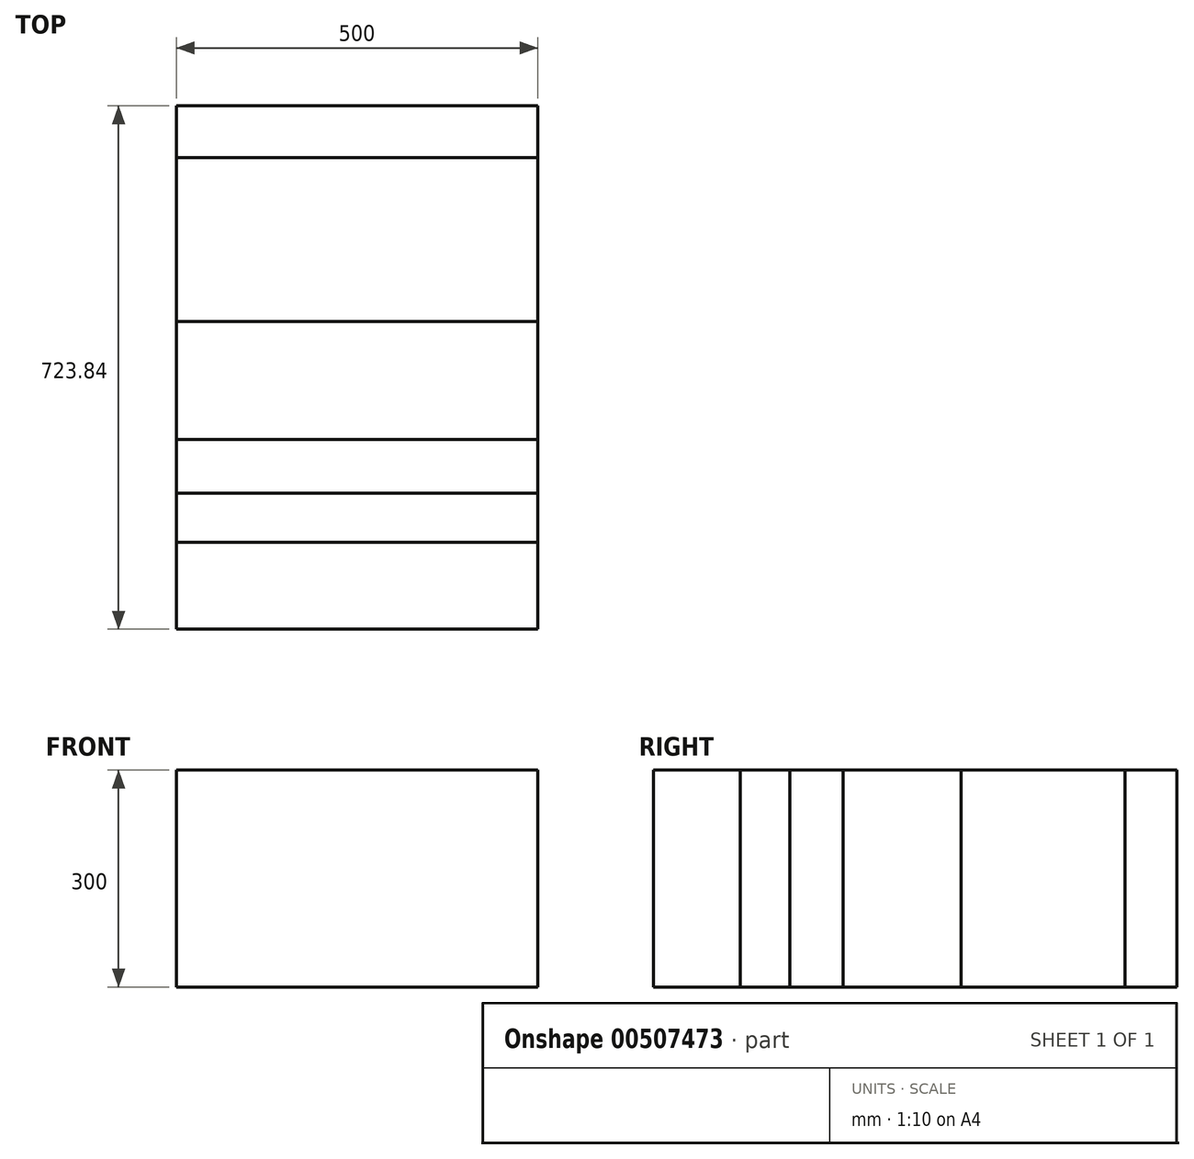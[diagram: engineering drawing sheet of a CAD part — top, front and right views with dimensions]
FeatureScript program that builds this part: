
annotation { "Feature Type Name" : "Feature", "Feature Type Description" : "" }
export const myFeature = defineFeature(function(context is Context, id is Id, definition is map)
    precondition{}
    {
        {
            var Q0;
            Q0=qCreatedBy(makeId("Right.planeOp"),FACE);
            var sketch = newSketch(context, id + "F0", { "sketchPlane" : qUnion([Q0])});
            skLineSegment(sketch, "E0.bottom", {"start": v(0, 217.8) * mm, "end": v(-71.76, 217.8) * mm});
            skLineSegment(sketch, "E0.top", {"start": v(0, -82.2) * mm, "end": v(-71.76, -82.2) * mm});
            skLineSegment(sketch, "E0.left", {"start": v(0, 217.8) * mm, "end": v(0, -82.2) * mm});
            skLineSegment(sketch, "E0.right", {"start": v(-71.76, 217.8) * mm, "end": v(-71.76, -82.2) * mm});
            skSolve(sketch);
        }
        {
            var Q0;
            Q0 = qSketchRegion(id + "F0", true);
            var sketch = newSketch(context, id + "F1", { "sketchPlane" : qUnion([Q0])});
            skLineSegment(sketch, "E1.bottom", {"start": v(-298.44, 217.8) * mm, "end": v(-71.76, 217.8) * mm});
            skLineSegment(sketch, "E1.top", {"start": v(-298.44, -82.2) * mm, "end": v(-71.76, -82.2) * mm});
            skLineSegment(sketch, "E1.left", {"start": v(-298.44, 217.8) * mm, "end": v(-298.44, -82.2) * mm});
            skLineSegment(sketch, "E1.right", {"start": v(-71.76, 217.8) * mm, "end": v(-71.76, -82.2) * mm});
            skLineSegment(sketch, "E2.bottom", {"start": v(-298.44, 217.8) * mm, "end": v(-461.65, 217.8) * mm});
            skLineSegment(sketch, "E2.top", {"start": v(-298.44, -82.2) * mm, "end": v(-461.65, -82.2) * mm});
            skLineSegment(sketch, "E2.right", {"start": v(-461.65, 217.8) * mm, "end": v(-461.65, -82.2) * mm});
            skLineSegment(sketch, "E3.bottom", {"start": v(-461.65, 217.8) * mm, "end": v(-535.58, 217.8) * mm});
            skLineSegment(sketch, "E3.top", {"start": v(-461.65, -82.2) * mm, "end": v(-535.58, -82.2) * mm});
            skLineSegment(sketch, "E3.right", {"start": v(-535.58, 217.8) * mm, "end": v(-535.58, -82.2) * mm});
            skLineSegment(sketch, "E4.bottom", {"start": v(-535.58, 217.8) * mm, "end": v(-603.68, 217.8) * mm});
            skLineSegment(sketch, "E4.top", {"start": v(-535.58, -82.2) * mm, "end": v(-603.68, -82.2) * mm});
            skLineSegment(sketch, "E4.right", {"start": v(-603.68, 217.8) * mm, "end": v(-603.68, -82.2) * mm});
            skLineSegment(sketch, "E5.bottom", {"start": v(-603.68, 217.8) * mm, "end": v(-723.84, 217.8) * mm});
            skLineSegment(sketch, "E5.top", {"start": v(-603.68, -82.2) * mm, "end": v(-723.84, -82.2) * mm});
            skLineSegment(sketch, "E5.right", {"start": v(-723.84, 217.8) * mm, "end": v(-723.84, -82.2) * mm});
            skSolve(sketch);
        }
        {
            var Q0;
            Q0=makeQuery(id+"F1.imprint","IMPRINT",FACE,{"disambiguationData":[TD([[makeQuery(id+"F1.imprint","IMPRINT",EDGE,{"derivedFrom":sQuery(id+"F1.wireOp",EDGE,"E2.bottom")}),1.0]])]});
            extrude(context, id + "F2", {"entities" : qUnion([Q0]), "depth" : 500 * mm, "symmetric" : true});
        }
        {
            var Q0;
            Q0=makeQuery(id+"F1.imprint","IMPRINT",FACE,{"disambiguationData":[TD([[makeQuery(id+"F1.imprint","IMPRINT",EDGE,{"derivedFrom":sQuery(id+"F1.wireOp",EDGE,"E3.bottom")}),1.0]])]});
            extrude(context, id + "F3", {"entities" : qUnion([Q0]), "depth" : 500 * mm, "symmetric" : true});
        }
        {
            var Q0;
            Q0=makeQuery(id+"F1.imprint","IMPRINT",FACE,{"disambiguationData":[TD([[makeQuery(id+"F1.imprint","IMPRINT",EDGE,{"derivedFrom":sQuery(id+"F1.wireOp",EDGE,"E4.bottom")}),1.0]])]});
            extrude(context, id + "F4", {"entities" : qUnion([Q0]), "depth" : 500 * mm, "symmetric" : true});
        }
        {
            var Q0;
            Q0=makeQuery(id+"F1.imprint","IMPRINT",FACE,{"disambiguationData":[TD([[makeQuery(id+"F1.imprint","IMPRINT",EDGE,{"derivedFrom":sQuery(id+"F1.wireOp",EDGE,"E5.bottom")}),1.0]])]});
            extrude(context, id + "F5", {"entities" : qUnion([Q0]), "depth" : 500 * mm, "symmetric" : true});
        }
        {
            var Q0;
            Q0=makeQuery(id+"F0.imprint","IMPRINT",FACE,{"disambiguationData":[TD([[makeQuery(id+"F0.imprint","IMPRINT",EDGE,{"derivedFrom":sQuery(id+"F0.wireOp",EDGE,"E0.bottom")}),1.0]])]});
            extrude(context, id + "F6", {"entities" : qUnion([Q0]), "depth" : 500 * mm, "symmetric" : true});
        }
        {
            var Q0;
            Q0=qCreatedBy(makeId("Right.planeOp"),FACE);
            var sketch = newSketch(context, id + "F7", { "sketchPlane" : qUnion([Q0])});
            skLineSegment(sketch, "E6", {"start": v(-544.73, 482.58) * mm, "end": v(-544.5, 482.58) * mm});
            skLineSegment(sketch, "E7", {"start": v(-544.48, 482.58) * mm, "end": v(-544.48, 482.34) * mm});
            skLineSegment(sketch, "E8", {"start": v(-544.48, 482.34) * mm, "end": v(-544.26, 482.59) * mm});
            skLineSegment(sketch, "E9", {"start": v(-543.41, 479.22) * mm, "end": v(-543.41, 479.22) * mm});
            skLineSegment(sketch, "E10", {"start": v(148.6, 413.4) * mm, "end": v(148.6, 524.4) * mm});
            skLineSegment(sketch, "E11", {"start": v(-455.02, 371.89) * mm, "end": v(-455.02, 520.96) * mm, "construction": true});
            skLineSegment(sketch, "E12", {"start": v(-386.58, 391.24) * mm, "end": v(-386.58, 519.74) * mm, "construction": true});
            skLineSegment(sketch, "E13", {"start": v(-537.77, 522.8) * mm, "end": v(-455.02, 520.96) * mm});
            skLineSegment(sketch, "E14", {"start": v(-574.7, 391.51) * mm, "end": v(-455.02, 391.16) * mm});
            skLineSegment(sketch, "E15", {"start": v(-149.14, 397.35) * mm, "end": v(76.9, 404.1) * mm});
            skLineSegment(sketch, "E16", {"start": v(185.78, 508.4) * mm, "end": v(186.03, 508.41) * mm});
            skLineSegment(sketch, "E17", {"start": v(185.9, 517.88) * mm, "end": v(185.9, 518.37) * mm});
            skLineSegment(sketch, "E18", {"start": v(185.9, 518.37) * mm, "end": v(185.64, 518.86) * mm});
            skLineSegment(sketch, "E19", {"start": v(185.64, 518.86) * mm, "end": v(185.4, 519.1) * mm});
            skLineSegment(sketch, "E20", {"start": v(185.4, 519.1) * mm, "end": v(185.16, 519.35) * mm});
            skLineSegment(sketch, "E21", {"start": v(186, 509) * mm, "end": v(185.9, 517.88) * mm});
            skLineSegment(sketch, "E22", {"start": v(184.81, 508.4) * mm, "end": v(179.48, 507.6) * mm});
            skLineSegment(sketch, "E23", {"start": v(179.48, 507.6) * mm, "end": v(174.38, 506.54) * mm});
            skLineSegment(sketch, "E24", {"start": v(174.38, 506.54) * mm, "end": v(169.53, 505.25) * mm});
            skLineSegment(sketch, "E25", {"start": v(169.53, 505.25) * mm, "end": v(164.46, 503.7) * mm});
            skLineSegment(sketch, "E26", {"start": v(184.81, 508.4) * mm, "end": v(185.06, 508.4) * mm});
            skLineSegment(sketch, "E27", {"start": v(185.06, 508.4) * mm, "end": v(185.3, 508.65) * mm});
            skLineSegment(sketch, "E28", {"start": v(185.3, 508.65) * mm, "end": v(185.77, 508.9) * mm});
            skLineSegment(sketch, "E29", {"start": v(185.77, 508.9) * mm, "end": v(185.77, 509.15) * mm});
            skLineSegment(sketch, "E30", {"start": v(185.77, 509.15) * mm, "end": v(186.01, 509.4) * mm});
            skLineSegment(sketch, "E31", {"start": v(186.01, 509.4) * mm, "end": v(186, 509.9) * mm});
            skLineSegment(sketch, "E32", {"start": v(164.46, 503.7) * mm, "end": v(161.07, 502.19) * mm});
            skLineSegment(sketch, "E33", {"start": v(161.07, 502.19) * mm, "end": v(157.7, 500.17) * mm});
            skLineSegment(sketch, "E34", {"start": v(157.7, 500.17) * mm, "end": v(154.55, 497.67) * mm});
            skLineSegment(sketch, "E35", {"start": v(154.55, 497.67) * mm, "end": v(152.17, 494.68) * mm});
            skLineSegment(sketch, "E36", {"start": v(152.17, 494.68) * mm, "end": v(150, 491.44) * mm});
            skLineSegment(sketch, "E37", {"start": v(150, 491.44) * mm, "end": v(148.6, 487.7) * mm});
            skLineSegment(sketch, "E38", {"start": v(185.16, 519.35) * mm, "end": v(181.97, 520.8) * mm});
            skLineSegment(sketch, "E39", {"start": v(181.97, 520.8) * mm, "end": v(179.05, 522) * mm});
            skLineSegment(sketch, "E40", {"start": v(179.05, 522) * mm, "end": v(175.64, 522.7) * mm});
            skLineSegment(sketch, "E41", {"start": v(175.64, 522.7) * mm, "end": v(172.47, 523.37) * mm});
            skLineSegment(sketch, "E42", {"start": v(172.47, 523.37) * mm, "end": v(169.07, 523.58) * mm});
            skLineSegment(sketch, "E43", {"start": v(169.07, 523.58) * mm, "end": v(165.65, 523.7) * mm});
            skLineSegment(sketch, "E44", {"start": v(-149.14, 397.35) * mm, "end": v(-149.14, 534.21) * mm, "construction": true});
            skLineSegment(sketch, "E45", {"start": v(-120.5, 533.08) * mm, "end": v(-45.95, 597.87) * mm});
            skLineSegment(sketch, "E46", {"start": v(64.59, 702.58) * mm, "end": v(101.77, 703.03) * mm});
            skLineSegment(sketch, "E47", {"start": v(95.44, 664.45) * mm, "end": v(101.77, 703.03) * mm});
            skLineSegment(sketch, "E48", {"start": v(61.9, 664.05) * mm, "end": v(95.44, 664.45) * mm});
            skLineSegment(sketch, "E49", {"start": v(61.9, 664.05) * mm, "end": v(66.93, 528.67) * mm});
            skLineSegment(sketch, "E50", {"start": v(66.93, 528.67) * mm, "end": v(118.28, 529.3) * mm});
            skLineSegment(sketch, "E51", {"start": v(-59.6, 601.16) * mm, "end": v(-53.01, 600.5) * mm});
            skLineSegment(sketch, "E52", {"start": v(-53.01, 600.5) * mm, "end": v(-46.7, 600.08) * mm});
            skLineSegment(sketch, "E53", {"start": v(-59.6, 601.16) * mm, "end": v(-59.38, 603.63) * mm});
            skLineSegment(sketch, "E54", {"start": v(-76.39, 603.67) * mm, "end": v(-59.38, 603.63) * mm});
            skLineSegment(sketch, "E55", {"start": v(-76.36, 601.2) * mm, "end": v(-59.35, 601.16) * mm});
            skLineSegment(sketch, "E56", {"start": v(-76.36, 601.2) * mm, "end": v(-76.39, 603.67) * mm});
            skLineSegment(sketch, "E57", {"start": v(-48.46, 605.49) * mm, "end": v(-51.38, 605.45) * mm});
            skLineSegment(sketch, "E58", {"start": v(-51.38, 605.45) * mm, "end": v(-54.06, 605.18) * mm});
            skLineSegment(sketch, "E59", {"start": v(-54.06, 605.18) * mm, "end": v(-56.71, 604.4) * mm});
            skLineSegment(sketch, "E60", {"start": v(-56.71, 604.4) * mm, "end": v(-59.38, 603.63) * mm});
            skLineSegment(sketch, "E61", {"start": v(-47.5, 606) * mm, "end": v(64.59, 702.58) * mm});
            skLineSegment(sketch, "E62", {"start": v(-48.46, 605.49) * mm, "end": v(-48.23, 605.5) * mm});
            skLineSegment(sketch, "E63", {"start": v(-48.23, 605.5) * mm, "end": v(-47.98, 605.74) * mm});
            skLineSegment(sketch, "E64", {"start": v(-47.98, 605.74) * mm, "end": v(-47.74, 605.75) * mm});
            skLineSegment(sketch, "E65", {"start": v(-47.74, 605.75) * mm, "end": v(-47.5, 606) * mm});
            skLineSegment(sketch, "E66", {"start": v(-45.95, 597.87) * mm, "end": v(-45.7, 598.37) * mm});
            skLineSegment(sketch, "E67", {"start": v(-45.7, 598.37) * mm, "end": v(-45.71, 598.61) * mm});
            skLineSegment(sketch, "E68", {"start": v(-45.71, 598.61) * mm, "end": v(-45.72, 598.86) * mm});
            skLineSegment(sketch, "E69", {"start": v(-45.72, 598.86) * mm, "end": v(-45.72, 599.35) * mm});
            skLineSegment(sketch, "E70", {"start": v(-45.72, 599.35) * mm, "end": v(-45.97, 599.6) * mm});
            skLineSegment(sketch, "E71", {"start": v(-45.97, 599.6) * mm, "end": v(-46.2, 599.84) * mm});
            skLineSegment(sketch, "E72", {"start": v(-46.2, 599.84) * mm, "end": v(-46.45, 600.08) * mm});
            skLineSegment(sketch, "E73", {"start": v(-46.45, 600.08) * mm, "end": v(-46.7, 600.08) * mm});
            skLineSegment(sketch, "E74", {"start": v(35.26, 677.3) * mm, "end": v(97.67, 678.05) * mm});
            skLineSegment(sketch, "E75", {"start": v(-823.38, 455.9) * mm, "end": v(148.6, 455.9) * mm, "construction": true});
            skLineSegment(sketch, "E76", {"start": v(76.9, 404.1) * mm, "end": v(76.9, 492.42) * mm, "construction": true});
            skLineSegment(sketch, "E77", {"start": v(-665.56, 391.08) * mm, "end": v(-574.7, 391.51) * mm});
            skLineSegment(sketch, "E78", {"start": v(-455.02, 391.16) * mm, "end": v(-386.58, 391.24) * mm});
            skLineSegment(sketch, "E79", {"start": v(-386.58, 391.24) * mm, "end": v(-312.7, 393.12) * mm});
            skLineSegment(sketch, "E80", {"start": v(76.9, 404.1) * mm, "end": v(148.6, 413.4) * mm});
            skLineSegment(sketch, "E81", {"start": v(-120.54, 533.04) * mm, "end": v(-45.95, 597.87) * mm});
            skLineSegment(sketch, "E82", {"start": v(95.44, 664.45) * mm, "end": v(119.07, 524.64) * mm});
            skLineSegment(sketch, "E83", {"start": v(66.93, 528.67) * mm, "end": v(118.21, 529.3) * mm});
            skLineSegment(sketch, "E84", {"start": v(-312.7, 366.48) * mm, "end": v(-312.7, 519.05) * mm, "construction": true});
            skLineSegment(sketch, "E85", {"start": v(-454.68, 410.4) * mm, "end": v(-148.5, 415.81) * mm});
            skLineSegment(sketch, "E86", {"start": v(-455.05, 482.68) * mm, "end": v(-150.92, 495.96) * mm});
            skLineSegment(sketch, "E87", {"start": v(-573.21, 404.77) * mm, "end": v(-454.68, 410.4) * mm});
            skLineSegment(sketch, "E88", {"start": v(-564.23, 487.04) * mm, "end": v(-544.3, 487.03) * mm});
            skLineSegment(sketch, "E89", {"start": v(-544.3, 487.03) * mm, "end": v(-455.16, 491.8) * mm});
            skLineSegment(sketch, "E90", {"start": v(-455.16, 491.8) * mm, "end": v(-387.23, 501.75) * mm});
            skLineSegment(sketch, "E91", {"start": v(-564.19, 483.83) * mm, "end": v(-564.23, 487.04) * mm});
            skLineSegment(sketch, "E92", {"start": v(-563.19, 400.95) * mm, "end": v(-543.75, 401.43) * mm});
            skLineSegment(sketch, "E93", {"start": v(-563.19, 400.95) * mm, "end": v(-563.24, 404.9) * mm});
            skLineSegment(sketch, "E94", {"start": v(-543.75, 401.43) * mm, "end": v(-453.37, 403.26) * mm});
            skLineSegment(sketch, "E95", {"start": v(-453.37, 403.26) * mm, "end": v(-385.57, 403.83) * mm});
            skLineSegment(sketch, "E96", {"start": v(-385.57, 403.83) * mm, "end": v(-267.87, 398.33) * mm});
            skLineSegment(sketch, "E97", {"start": v(-387.23, 501.75) * mm, "end": v(-117.7, 502.53) * mm});
            skLineSegment(sketch, "E98", {"start": v(-117.7, 502.53) * mm, "end": v(76.9, 507.59) * mm});
            skLineSegment(sketch, "E99", {"start": v(76.9, 507.59) * mm, "end": v(184.81, 508.4) * mm});
            skLineSegment(sketch, "E100", {"start": v(-563.24, 405.39) * mm, "end": v(-564.19, 483.83) * mm});
            skLineSegment(sketch, "E101", {"start": v(-386.89, 493.86) * mm, "end": v(-313.11, 501.9) * mm});
            skLineSegment(sketch, "E102", {"start": v(-530.49, 469.18) * mm, "end": v(-533.38, 467.91) * mm});
            skLineSegment(sketch, "E103", {"start": v(-534.35, 467.66) * mm, "end": v(-535.3, 467.15) * mm});
            skLineSegment(sketch, "E104", {"start": v(-535.3, 467.15) * mm, "end": v(-537, 466.14) * mm});
            skLineSegment(sketch, "E105", {"start": v(-537.73, 465.89) * mm, "end": v(-539.9, 464.63) * mm});
            skLineSegment(sketch, "E106", {"start": v(-539.9, 464.63) * mm, "end": v(-540.39, 464.37) * mm});
            skLineSegment(sketch, "E107", {"start": v(-541.1, 463.87) * mm, "end": v(-543.76, 462.36) * mm});
            skLineSegment(sketch, "E108", {"start": v(-544.48, 461.86) * mm, "end": v(-546.9, 460.1) * mm});
            skLineSegment(sketch, "E109", {"start": v(-547.63, 459.6) * mm, "end": v(-548.83, 458.84) * mm});
            skLineSegment(sketch, "E110", {"start": v(-548.83, 458.84) * mm, "end": v(-550.02, 457.84) * mm});
            skLineSegment(sketch, "E111", {"start": v(-550.75, 457.1) * mm, "end": v(-552.92, 455.59) * mm});
            skLineSegment(sketch, "E112", {"start": v(-552.92, 455.59) * mm, "end": v(-553.16, 455.34) * mm});
            skLineSegment(sketch, "E113", {"start": v(-553.88, 454.59) * mm, "end": v(-556.04, 452.59) * mm});
            skLineSegment(sketch, "E114", {"start": v(-556.77, 452.09) * mm, "end": v(-558.68, 449.84) * mm});
            skLineSegment(sketch, "E115", {"start": v(-559.4, 449.1) * mm, "end": v(-560.36, 448.1) * mm});
            skLineSegment(sketch, "E116", {"start": v(-560.36, 448.1) * mm, "end": v(-561.3, 446.85) * mm});
            skLineSegment(sketch, "E117", {"start": v(-562.04, 446.12) * mm, "end": v(-563.7, 444.12) * mm});
            skLineSegment(sketch, "E118", {"start": v(-563.7, 444.12) * mm, "end": v(-561.98, 441.43) * mm});
            skLineSegment(sketch, "E119", {"start": v(-561.48, 440.7) * mm, "end": v(-561.23, 440.2) * mm});
            skLineSegment(sketch, "E120", {"start": v(-561.23, 440.2) * mm, "end": v(-559.51, 438.25) * mm});
            skLineSegment(sketch, "E121", {"start": v(-559.01, 437.52) * mm, "end": v(-558.28, 436.54) * mm});
            skLineSegment(sketch, "E122", {"start": v(-558.28, 436.54) * mm, "end": v(-557.05, 435.32) * mm});
            skLineSegment(sketch, "E123", {"start": v(-556.31, 434.59) * mm, "end": v(-555.08, 433.12) * mm});
            skLineSegment(sketch, "E124", {"start": v(-555.08, 433.12) * mm, "end": v(-554.33, 432.4) * mm});
            skLineSegment(sketch, "E125", {"start": v(-553.6, 431.66) * mm, "end": v(-551.9, 430.2) * mm});
            skLineSegment(sketch, "E126", {"start": v(-551.9, 430.2) * mm, "end": v(-551.4, 429.71) * mm});
            skLineSegment(sketch, "E127", {"start": v(-550.66, 429.23) * mm, "end": v(-548.45, 427.28) * mm});
            skLineSegment(sketch, "E128", {"start": v(-547.7, 426.8) * mm, "end": v(-545.25, 425.1) * mm});
            skLineSegment(sketch, "E129", {"start": v(-544.28, 424.62) * mm, "end": v(-541.83, 423.16) * mm});
            skLineSegment(sketch, "E130", {"start": v(-540.85, 422.68) * mm, "end": v(-540.36, 422.44) * mm});
            skLineSegment(sketch, "E131", {"start": v(-540.36, 422.44) * mm, "end": v(-538.16, 421.48) * mm});
            skLineSegment(sketch, "E132", {"start": v(-537.43, 421) * mm, "end": v(-536.21, 420.52) * mm});
            skLineSegment(sketch, "E133", {"start": v(-536.21, 420.52) * mm, "end": v(-534.74, 420.04) * mm});
            skLineSegment(sketch, "E134", {"start": v(-533.77, 419.8) * mm, "end": v(-531.82, 419.1) * mm});
            skLineSegment(sketch, "E135", {"start": v(-531.82, 419.1) * mm, "end": v(-531.08, 418.85) * mm});
            skLineSegment(sketch, "E136", {"start": v(-530.1, 418.62) * mm, "end": v(-527.44, 417.91) * mm});
            skLineSegment(sketch, "E137", {"start": v(-532.67, 468.9) * mm, "end": v(-386.89, 493.86) * mm});
            skLineSegment(sketch, "E138", {"start": v(-527.18, 417.17) * mm, "end": v(-385.57, 403.83) * mm});
            skLineSegment(sketch, "E139", {"start": v(-149.23, 496.23) * mm, "end": v(149.78, 491.2) * mm});
            skLineSegment(sketch, "E140", {"start": v(34.38, 676.55) * mm, "end": v(93.34, 677.26) * mm});
            skLineSegment(sketch, "E141", {"start": v(93.34, 677.26) * mm, "end": v(95.44, 664.45) * mm});
            skLineSegment(sketch, "E142", {"start": v(-675.84, 498.77) * mm, "end": v(-658.22, 367.5) * mm, "construction": true});
            skLineSegment(sketch, "E143", {"start": v(-578.4, 476.5) * mm, "end": v(-578.4, 476.5) * mm});
            skLineSegment(sketch, "E144", {"start": v(-592.82, 510.6) * mm, "end": v(-577.84, 477.45) * mm});
            skLineSegment(sketch, "E145", {"start": v(-577.68, 480.7) * mm, "end": v(-569.43, 482.53) * mm});
            skLineSegment(sketch, "E146", {"start": v(-524.47, 492.36) * mm, "end": v(-517.58, 522.34) * mm});
            skLineSegment(sketch, "E147", {"start": v(-519.53, 487.1) * mm, "end": v(-511.45, 522.2) * mm});
            skLineSegment(sketch, "E148", {"start": v(-655.74, 477.05) * mm, "end": v(-596.24, 508.84) * mm});
            skLineSegment(sketch, "E149", {"start": v(-653.08, 478.56) * mm, "end": v(-652.58, 476.35) * mm});
            skLineSegment(sketch, "E150", {"start": v(-652.58, 476.35) * mm, "end": v(-651.81, 474.38) * mm});
            skLineSegment(sketch, "E151", {"start": v(-651.81, 474.38) * mm, "end": v(-651.07, 472.42) * mm});
            skLineSegment(sketch, "E152", {"start": v(-651.07, 472.42) * mm, "end": v(-650.08, 470.46) * mm});
            skLineSegment(sketch, "E153", {"start": v(-650.08, 470.46) * mm, "end": v(-649.83, 470.21) * mm});
            skLineSegment(sketch, "E154", {"start": v(-649.83, 470.21) * mm, "end": v(-649.58, 470.22) * mm});
            skLineSegment(sketch, "E155", {"start": v(-655.74, 477.05) * mm, "end": v(-654.74, 474.1) * mm});
            skLineSegment(sketch, "E156", {"start": v(-654.74, 474.1) * mm, "end": v(-653.49, 471.16) * mm});
            skLineSegment(sketch, "E157", {"start": v(-653.49, 471.16) * mm, "end": v(-652.24, 468.46) * mm});
            skLineSegment(sketch, "E158", {"start": v(-652.24, 468.46) * mm, "end": v(-650.5, 465.76) * mm});
            skLineSegment(sketch, "E159", {"start": v(-650.5, 465.76) * mm, "end": v(-650.27, 465.77) * mm});
            skLineSegment(sketch, "E160", {"start": v(-650.27, 465.77) * mm, "end": v(-650.26, 465.52) * mm});
            skLineSegment(sketch, "E161", {"start": v(-650.26, 465.52) * mm, "end": v(-650.02, 465.52) * mm});
            skLineSegment(sketch, "E162", {"start": v(-148.96, 413.83) * mm, "end": v(77.5, 417.55) * mm});
            skLineSegment(sketch, "E163", {"start": v(-148.89, 407.66) * mm, "end": v(77.58, 411.62) * mm});
            skLineSegment(sketch, "E164", {"start": v(-312.25, 410.88) * mm, "end": v(-148.48, 413.84) * mm});
            skLineSegment(sketch, "E165", {"start": v(-312.17, 404.96) * mm, "end": v(-148.4, 407.67) * mm});
            skLineSegment(sketch, "E166", {"start": v(-530.2, 466.47) * mm, "end": v(-313.28, 456) * mm});
            skLineSegment(sketch, "E167", {"start": v(-529.78, 472.4) * mm, "end": v(-313.1, 461.93) * mm});
            skLineSegment(sketch, "E168", {"start": v(-530.2, 466.47) * mm, "end": v(-529.78, 472.4) * mm});
            skLineSegment(sketch, "E169", {"start": v(-313.28, 456) * mm, "end": v(-313.1, 461.93) * mm});
            skPoint(sketch, "E170", {"position": v(-149.14, 455.9) * mm});
            skPoint(sketch, "E171", {"position": v(76.9, 455.9) * mm});
            skPoint(sketch, "E172", {"position": v(-312.7, 455.9) * mm});
            skPoint(sketch, "E173", {"position": v(-386.58, 455.9) * mm});
            skPoint(sketch, "E174", {"position": v(-455.02, 455.9) * mm});
            skPoint(sketch, "E175", {"position": v(-574.7, 455.9) * mm});
            skPoint(sketch, "E176", {"position": v(-670.09, 455.9) * mm});
            skLineSegment(sketch, "E177", {"start": v(-574.7, 391.51) * mm, "end": v(-574.7, 517.74) * mm, "construction": true});
            skArc(sketch, "E178", {"start": v(-537.77, 522.8) * mm, "mid": v(-567.9, 519.58) * mm, "end": v(-596.24, 508.84) * mm});
            skLineSegment(sketch, "E179.trimOffspring", {"start": v(-569.7, 482.47) * mm, "end": v(-455.2, 482.68) * mm});
            skPoint(sketch, "E180", {"position": v(-517.58, 522.34) * mm});
            skPoint(sketch, "E181", {"position": v(-511.45, 522.2) * mm});
            skPoint(sketch, "E182", {"position": v(-592.82, 510.6) * mm});
            skLineSegment(sketch, "E183", {"start": v(-587.38, 513.1) * mm, "end": v(-574.27, 484.12) * mm});
            skLineSegment(sketch, "E184", {"start": v(-519.53, 487.1) * mm, "end": v(-650.02, 465.52) * mm});
            skPoint(sketch, "E185", {"position": v(-574.7, 477.97) * mm});
            skLineSegment(sketch, "E186.trimOffspring", {"start": v(-574.27, 484.12) * mm, "end": v(-524.47, 492.36) * mm});
            skLineSegment(sketch, "E187", {"start": v(-598.15, 507.81) * mm, "end": v(-586.52, 482.1) * mm});
            skLineSegment(sketch, "E188", {"start": v(-586.52, 482.1) * mm, "end": v(-644.06, 472.59) * mm});
            skFitSpline(sketch, "E189", {"points": [v(-823.38, 411.14) * mm, v(-749.3, 395) * mm, v(-665.4, 391.08) * mm], "startDerivative": vector(235.8, -73.27) * mm, "endDerivative": vector(166.57, -1.13) * mm});
            skFitSpline(sketch, "E190", {"points": [v(-823.38, 411.14) * mm, v(-672.04, 470.45) * mm, v(-655.74, 477.05) * mm], "startDerivative": vector(194.65, 135.25) * mm, "endDerivative": vector(107.55, 61.1) * mm});
            skLineSegment(sketch, "E191", {"start": v(-455.02, 520.96) * mm, "end": v(-386.58, 519.74) * mm});
            skLineSegment(sketch, "E192", {"start": v(-386.58, 519.74) * mm, "end": v(-312.7, 519.05) * mm});
            skLineSegment(sketch, "E193", {"start": v(-312.7, 519.05) * mm, "end": v(-149.14, 534.21) * mm});
            skLineSegment(sketch, "E194", {"start": v(-149.14, 534.21) * mm, "end": v(76.9, 524.98) * mm});
            skLineSegment(sketch, "E195", {"start": v(76.9, 524.98) * mm, "end": v(148.6, 524.4) * mm});
            skLineSegment(sketch, "E196", {"start": v(148.6, 524.4) * mm, "end": v(165.65, 523.7) * mm});
            skLineSegment(sketch, "E197", {"start": v(-312.7, 393.12) * mm, "end": v(-149.14, 397.35) * mm});
            skLineSegment(sketch, "E198.trimOffspring", {"start": v(76.9, 507.59) * mm, "end": v(76.9, 524.98) * mm});
            skSolve(sketch);
        }
        {
            var Q0;
            Q0=makeQuery(id+"F1.imprint","IMPRINT",FACE,{"disambiguationData":[TD([[makeQuery(id+"F1.imprint","IMPRINT",EDGE,{"derivedFrom":sQuery(id+"F1.wireOp",EDGE,"E1.bottom")}),-1.0]])]});
            extrude(context, id + "F8", {"entities" : qUnion([Q0]), "depth" : 500 * mm, "symmetric" : true});
        }
    });
